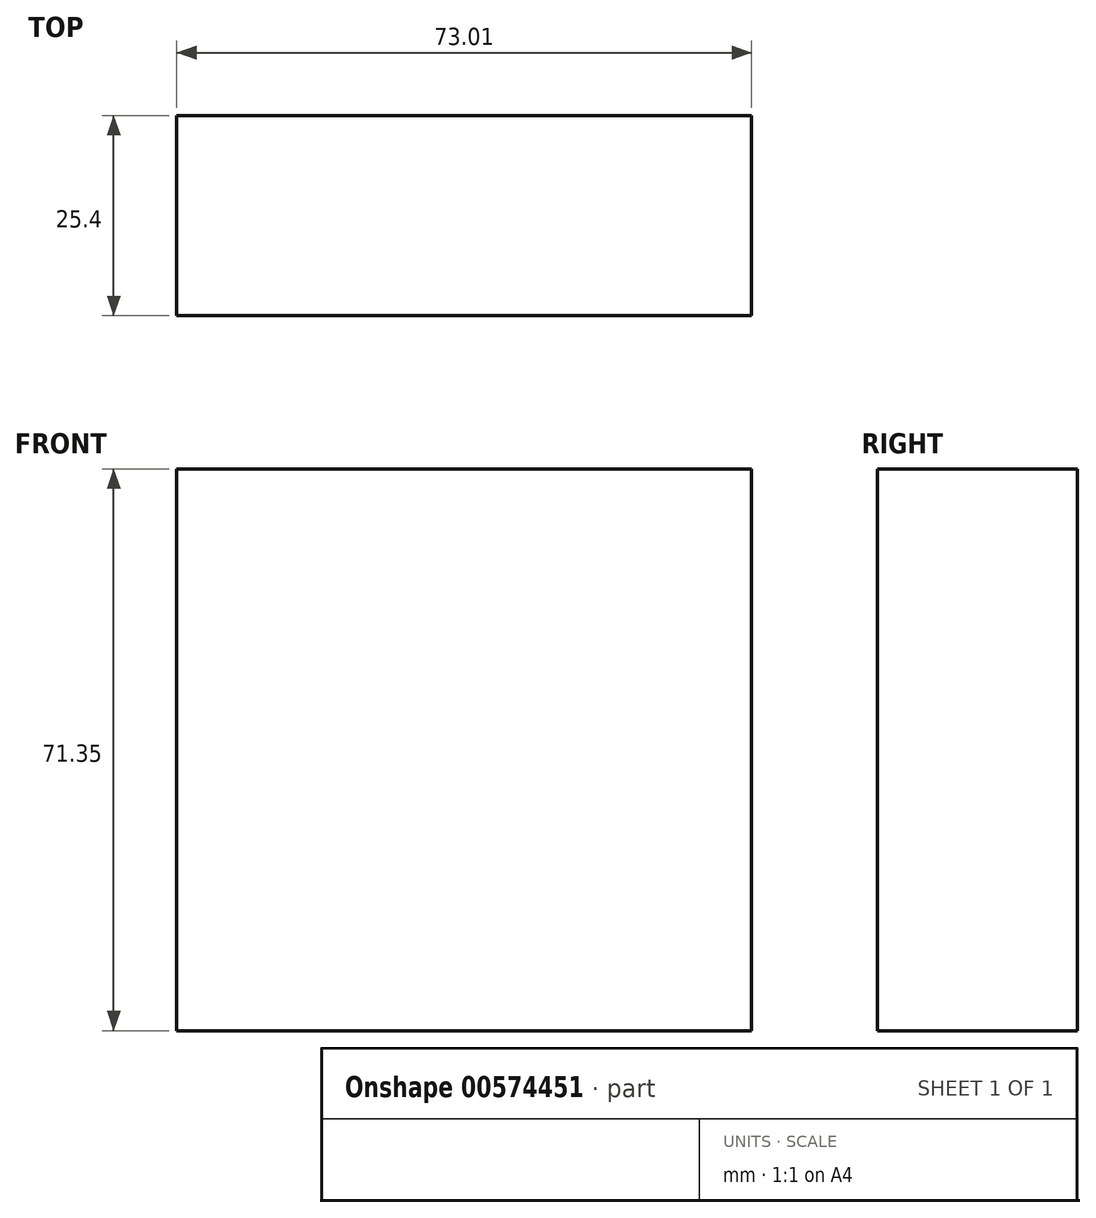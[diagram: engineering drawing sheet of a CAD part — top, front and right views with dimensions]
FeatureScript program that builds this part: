
annotation { "Feature Type Name" : "Feature", "Feature Type Description" : "" }
export const myFeature = defineFeature(function(context is Context, id is Id, definition is map)
    precondition{}
    {
        {
            var Q0;
            Q0=qCreatedBy(makeId("Front.planeOp"),FACE);
            var sketch = newSketch(context, id + "F0", { "sketchPlane" : qUnion([Q0])});
            skLineSegment(sketch, "E0.bottom", {"start": v(-62.27, 71.35) * mm, "end": v(10.74, 71.35) * mm});
            skLineSegment(sketch, "E0.top", {"start": v(-62.27, 0) * mm, "end": v(10.74, 0) * mm});
            skLineSegment(sketch, "E0.left", {"start": v(-62.27, 71.35) * mm, "end": v(-62.27, 0) * mm});
            skLineSegment(sketch, "E0.right", {"start": v(10.74, 71.35) * mm, "end": v(10.74, 0) * mm});
            skSolve(sketch);
        }
        {
            var Q0;
            Q0=makeQuery(id+"F0.imprint","IMPRINT",FACE,{"disambiguationData":[TD([[makeQuery(id+"F0.imprint","IMPRINT",EDGE,{"derivedFrom":sQuery(id+"F0.wireOp",EDGE,"E0.bottom")}),-1.0]])]});
            extrude(context, id + "F1", {"entities" : qUnion([Q0]), "depth" : 25.4 * mm, "offsetDistance" : 25.4 * mm});
        }
    });
